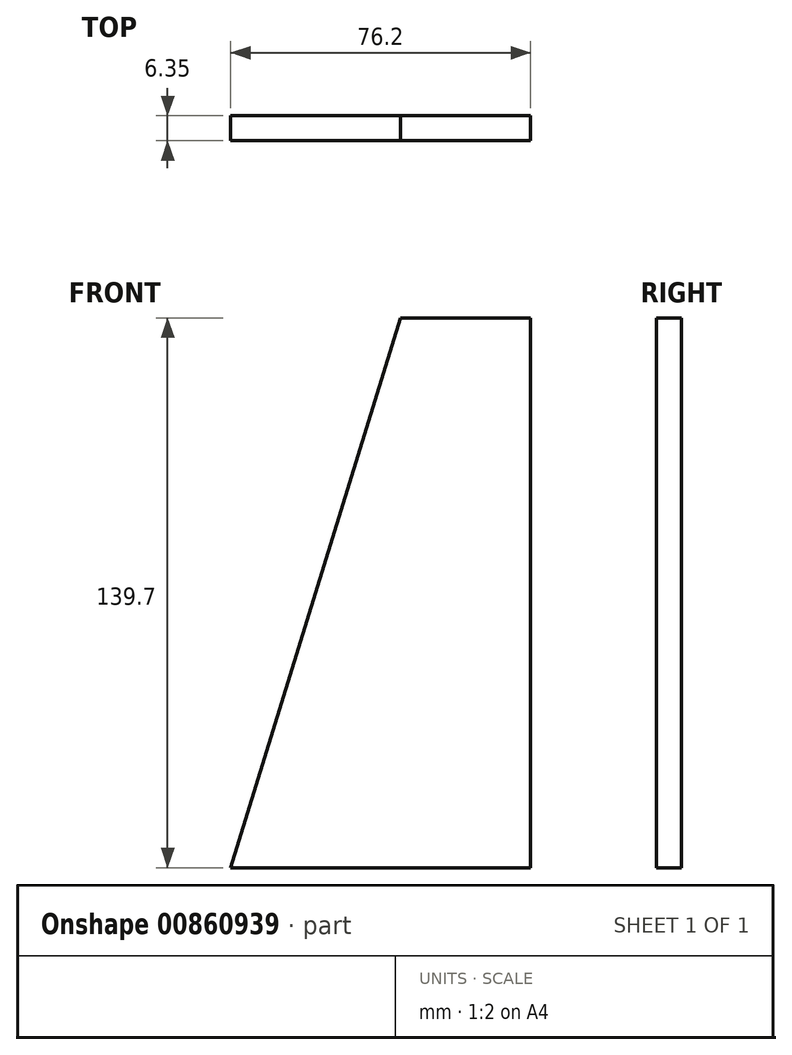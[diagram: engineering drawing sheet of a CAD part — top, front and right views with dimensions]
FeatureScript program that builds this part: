
annotation { "Feature Type Name" : "Feature", "Feature Type Description" : "" }
export const myFeature = defineFeature(function(context is Context, id is Id, definition is map)
    precondition{}
    {
        {
            var Q0;
            Q0=qCreatedBy(makeId("Front.planeOp"),FACE);
            var sketch = newSketch(context, id + "F0", { "sketchPlane" : qUnion([Q0])});
            skLineSegment(sketch, "E0.bottom", {"start": v(8.14, 66.7) * mm, "end": v(41.16, 66.7) * mm});
            skLineSegment(sketch, "E0.top", {"start": v(-35.04, -73) * mm, "end": v(41.16, -73) * mm});
            skLineSegment(sketch, "E0.right", {"start": v(41.16, 66.7) * mm, "end": v(41.16, -73) * mm});
            skLineSegment(sketch, "E1", {"start": v(-35.04, -73) * mm, "end": v(8.14, 66.7) * mm});
            skSolve(sketch);
        }
        {
            var Q0;
            Q0 = qSketchRegion(id + "F0", true);
            extrude(context, id + "F1", {"entities" : qUnion([Q0]), "depth" : 6.35 * mm, "offsetDistance" : 25.4 * mm});
        }
    });
